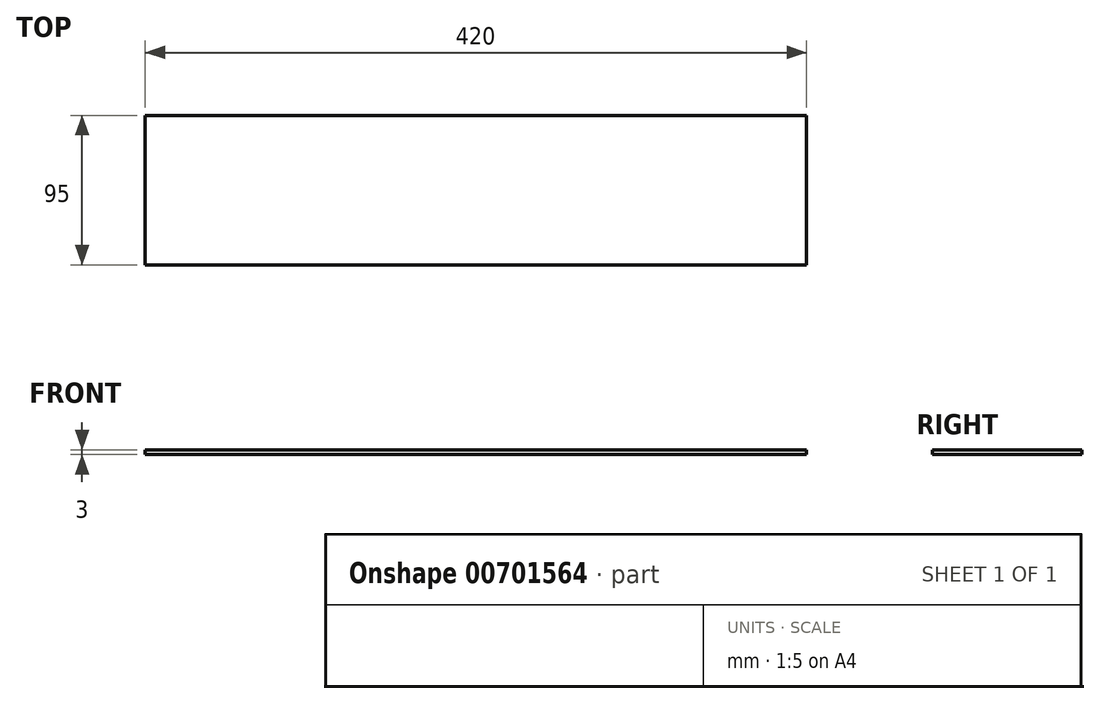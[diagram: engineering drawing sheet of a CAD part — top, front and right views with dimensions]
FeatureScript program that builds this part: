
annotation { "Feature Type Name" : "Feature", "Feature Type Description" : "" }
export const myFeature = defineFeature(function(context is Context, id is Id, definition is map)
    precondition{}
    {
        {
            var Q0;
            Q0=qCreatedBy(makeId("Top.planeOp"),FACE);
            var sketch = newSketch(context, id + "F0", { "sketchPlane" : qUnion([Q0])});
            skLineSegment(sketch, "E0.bottom", {"start": v(210, 47.5) * mm, "end": v(-210, 47.5) * mm});
            skLineSegment(sketch, "E0.top", {"start": v(210, -47.5) * mm, "end": v(-210, -47.5) * mm});
            skLineSegment(sketch, "E0.left", {"start": v(210, 47.5) * mm, "end": v(210, -47.5) * mm});
            skLineSegment(sketch, "E0.right", {"start": v(-210, 47.5) * mm, "end": v(-210, -47.5) * mm});
            skPoint(sketch, "E0.middle", {"position": v(0, 0) * mm});
            skSolve(sketch);
        }
        {
            var Q0;
            Q0=makeQuery(id+"F0.imprint","IMPRINT",FACE,{"disambiguationData":[TD([[makeQuery(id+"F0.imprint","IMPRINT",EDGE,{"derivedFrom":sQuery(id+"F0.wireOp",EDGE,"E0.bottom")}),1.0]])]});
            extrude(context, id + "F1", {"entities" : qUnion([Q0]), "depth" : 3 * mm, "offsetDistance" : 25 * mm});
        }
    });
